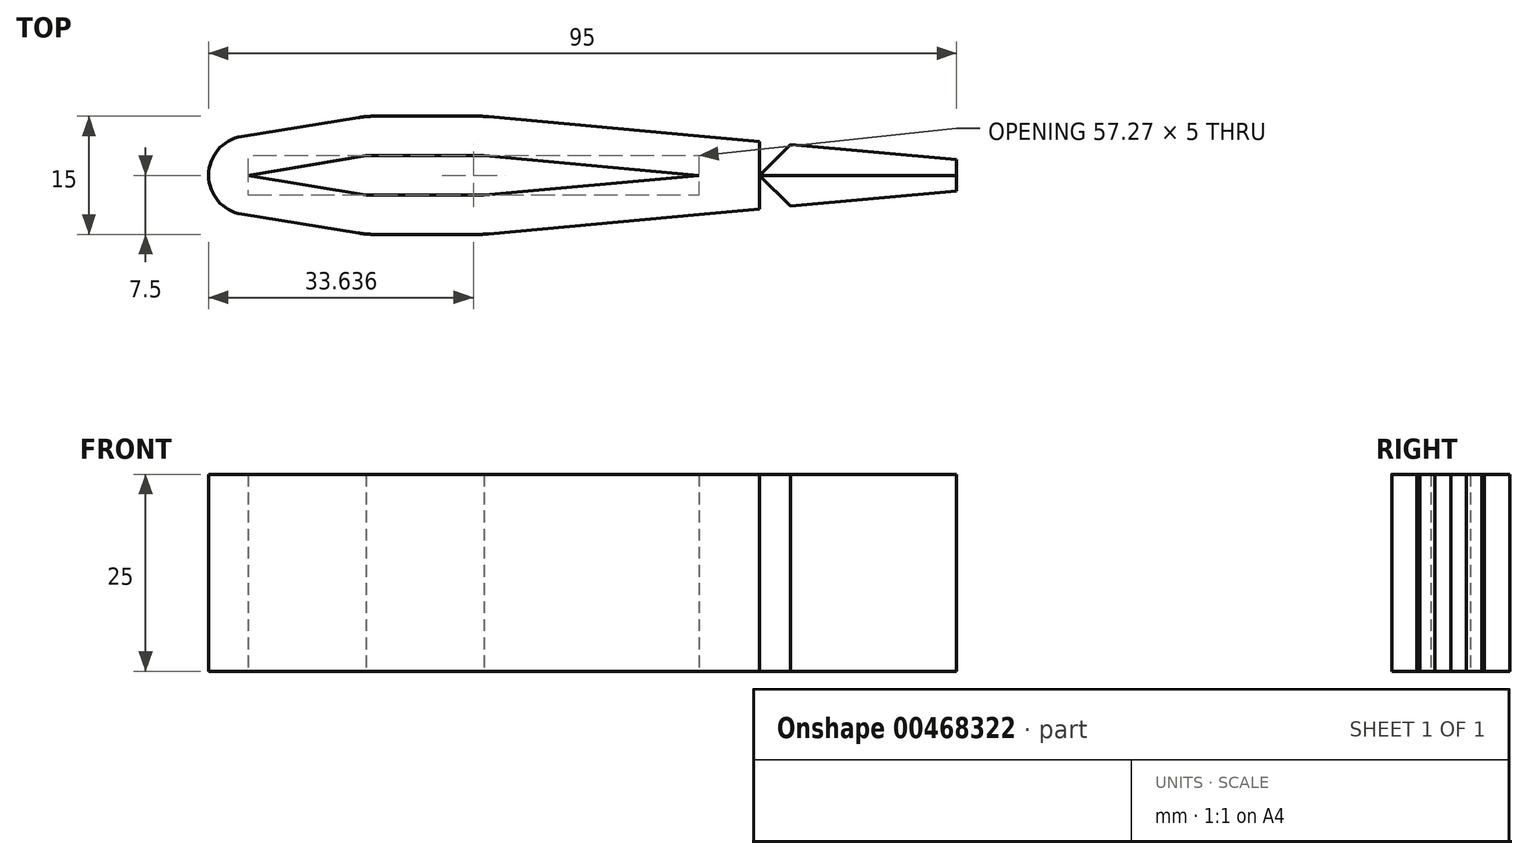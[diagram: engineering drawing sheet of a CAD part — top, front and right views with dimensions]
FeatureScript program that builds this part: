
annotation { "Feature Type Name" : "Feature", "Feature Type Description" : "" }
export const myFeature = defineFeature(function(context is Context, id is Id, definition is map)
    precondition{}
    {
        {
            var Q0;
            Q0=qCreatedBy(makeId("Top.planeOp"),FACE);
            var sketch = newSketch(context, id + "F0", { "sketchPlane" : qUnion([Q0])});
            skArc(sketch, "E0", {"start": v(19.2, 4.94) * mm, "mid": v(15, 0) * mm, "end": v(19.2, -4.94) * mm});
            skLineSegment(sketch, "E1", {"start": v(20, 0) * mm, "end": v(110, 0) * mm});
            skLineSegment(sketch, "E2", {"start": v(19.2, 4.94) * mm, "end": v(34.04, 7.34) * mm});
            skLineSegment(sketch, "E3", {"start": v(77.27, 5) * mm, "end": v(110, 2) * mm});
            skLineSegment(sketch, "E4", {"start": v(110, 2) * mm, "end": v(110, -2) * mm});
            skLineSegment(sketch, "E5", {"start": v(77.27, -5) * mm, "end": v(110, -2) * mm});
            skLineSegment(sketch, "E6", {"start": v(77.27, -5) * mm, "end": v(50.55, -7.45) * mm});
            skLineSegment(sketch, "E7.bottom", {"start": v(51.5, -42.46) * mm, "end": v(83.85, -42.46) * mm});
            skLineSegment(sketch, "E7.top", {"start": v(51.5, -38.46) * mm, "end": v(83.85, -38.46) * mm});
            skLineSegment(sketch, "E7.left", {"start": v(51.5, -42.46) * mm, "end": v(51.5, -38.46) * mm});
            skLineSegment(sketch, "E7.right", {"start": v(83.85, -42.46) * mm, "end": v(83.85, -38.46) * mm});
            skLineSegment(sketch, "E8", {"start": v(67.67, -42.46) * mm, "end": v(71.67, -38.46) * mm});
            skLineSegment(sketch, "E9", {"start": v(71.67, -38.46) * mm, "end": v(67.67, -42.46) * mm});
            skLineSegment(sketch, "E10", {"start": v(67.67, -42.46) * mm, "end": v(63.67, -38.46) * mm});
            skLineSegment(sketch, "E11.bottom", {"start": v(50, -2.5) * mm, "end": v(35, -2.5) * mm});
            skLineSegment(sketch, "E11.top", {"start": v(50, 2.5) * mm, "end": v(35, 2.5) * mm});
            skLineSegment(sketch, "E11.left", {"start": v(50, -2.5) * mm, "end": v(50, 2.5) * mm});
            skLineSegment(sketch, "E11.right", {"start": v(35, -2.5) * mm, "end": v(35, 2.5) * mm});
            skPoint(sketch, "E11.middle", {"position": v(42.5, 0) * mm});
            skLineSegment(sketch, "E12", {"start": v(35.97, 7.5) * mm, "end": v(49.45, 7.5) * mm});
            skLineSegment(sketch, "E13", {"start": v(50.55, 7.45) * mm, "end": v(77.27, 5) * mm});
            skLineSegment(sketch, "E14", {"start": v(49.45, -7.5) * mm, "end": v(35.97, -7.5) * mm});
            skLineSegment(sketch, "E15", {"start": v(34.04, -7.34) * mm, "end": v(19.2, -4.94) * mm});
            skLineSegment(sketch, "E16", {"start": v(35, 2.5) * mm, "end": v(35, 7.5) * mm, "construction": true});
            skLineSegment(sketch, "E17", {"start": v(77.27, 0) * mm, "end": v(77.27, 5) * mm, "construction": true});
            skLineSegment(sketch, "E18", {"start": v(77.27, -5) * mm, "end": v(77.27, 0) * mm, "construction": true});
            skLineSegment(sketch, "E19", {"start": v(35, -7.5) * mm, "end": v(35, -2.5) * mm, "construction": true});
            skLineSegment(sketch, "E20", {"start": v(20, 0) * mm, "end": v(15, 0) * mm, "construction": true});
            skLineSegment(sketch, "E21", {"start": v(20, 0) * mm, "end": v(35, 2.5) * mm});
            skLineSegment(sketch, "E22", {"start": v(50, 2.5) * mm, "end": v(77.27, 0) * mm});
            skLineSegment(sketch, "E23", {"start": v(50, -2.5) * mm, "end": v(77.27, 0) * mm});
            skLineSegment(sketch, "E24", {"start": v(35, -2.5) * mm, "end": v(20, 0) * mm});
            skLineSegment(sketch, "E25", {"start": v(85, 4.3) * mm, "end": v(85, -4.3) * mm});
            skLineSegment(sketch, "E26", {"start": v(85, 0) * mm, "end": v(88.93, -3.93) * mm});
            skLineSegment(sketch, "E27", {"start": v(85, 0) * mm, "end": v(88.93, 3.93) * mm});
            skPoint(sketch, "E28.visualSharp", {"position": v(35, 7.5) * mm});
            skArc(sketch, "E28.filletArc", {"start": v(35.97, 7.5) * mm, "mid": v(35, 7.46) * mm, "end": v(34.04, 7.34) * mm});
            skPoint(sketch, "E29.visualSharp", {"position": v(35, -7.5) * mm});
            skArc(sketch, "E29.filletArc", {"start": v(34.04, -7.34) * mm, "mid": v(35, -7.46) * mm, "end": v(35.97, -7.5) * mm});
            skPoint(sketch, "E30.visualSharp", {"position": v(50, -7.5) * mm});
            skArc(sketch, "E30.filletArc", {"start": v(49.45, -7.5) * mm, "mid": v(50, -7.49) * mm, "end": v(50.55, -7.45) * mm});
            skPoint(sketch, "E31.visualSharp", {"position": v(50, 7.5) * mm});
            skArc(sketch, "E31.filletArc", {"start": v(50.55, 7.45) * mm, "mid": v(50, 7.49) * mm, "end": v(49.45, 7.5) * mm});
            skLineSegment(sketch, "E32", {"start": v(50, 2.5) * mm, "end": v(50.39, 7.46) * mm, "construction": true});
            skSolve(sketch);
        }
        {
            var Q0;
            Q0=makeQuery(id+"F0.imprint","IMPRINT",FACE,{"disambiguationData":[TD([[makeQuery(id+"F0.imprint","IMPRINT",EDGE,{"derivedFrom":sQuery(id+"F0.wireOp",EDGE,"E0")}),1.0]])]});
            var Q1;
            {var subQ3=sQuery(id+"F0.wireOp",EDGE,"E26");Q1=makeQuery(id+"F0.imprint","IMPRINT",FACE,{"disambiguationData":[TD([[makeQuery(id+"F0.imprint","IMPRINT",EDGE,{"derivedFrom":subQ3}),1.0]])]});}
            var Q2;
            {var subQ3=sQuery(id+"F0.wireOp",EDGE,"E27");Q2=makeQuery(id+"F0.imprint","IMPRINT",FACE,{"disambiguationData":[TD([[makeQuery(id+"F0.imprint","IMPRINT",EDGE,{"derivedFrom":subQ3}),-1.0]])]});}
            extrude(context, id + "F1", {"entities" : qUnion([Q0, Q1, Q2]), "depth" : 25 * mm, "offsetDistance" : 25 * mm});
        }
    });
